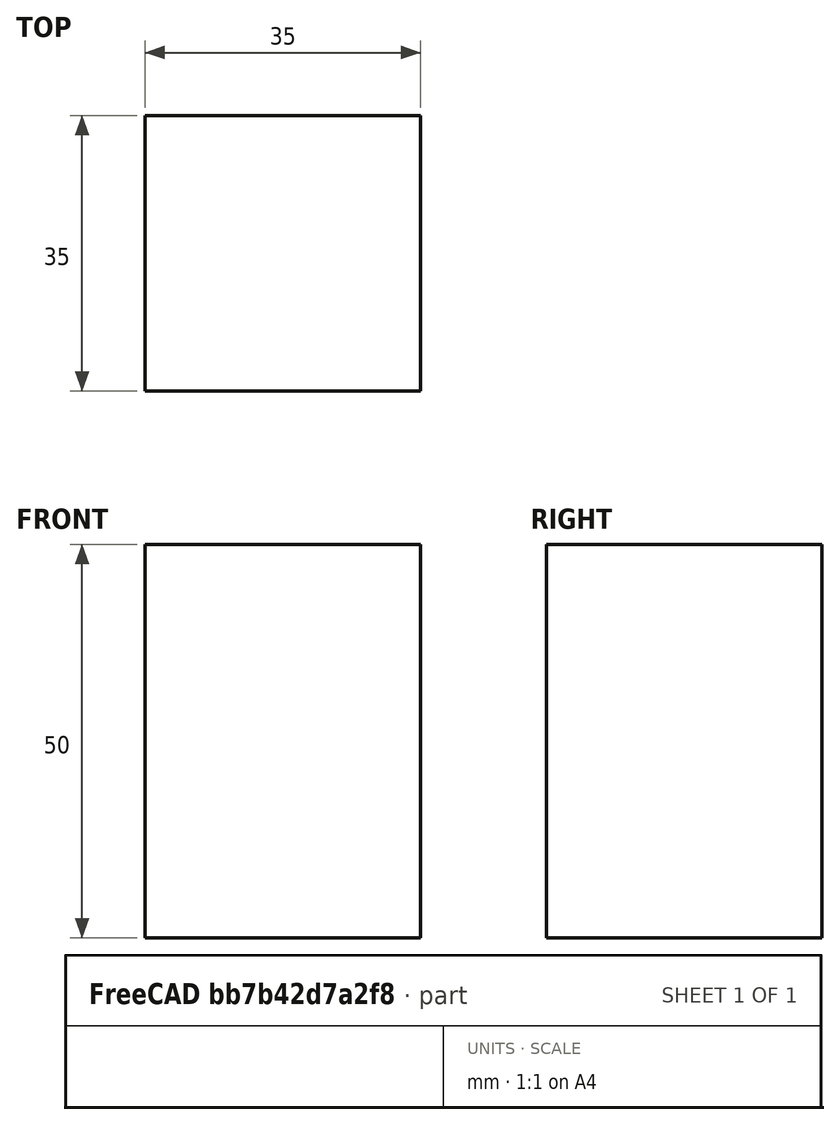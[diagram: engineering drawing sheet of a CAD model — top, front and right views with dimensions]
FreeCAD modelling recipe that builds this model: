
FCSTD DOCUMENT  (FreeCAD 0.15R4671 (Git))
Label: Square Bar 35 EN10059 S235JR
License: All rights reserved
LicenseURL: http://en.wikipedia.org/wiki/All_rights_reserved
objects: Sketcher::SketchObject×1, Part::Extrusion×1
note: 2 computed .brp shape members not serialized (recipe doc carries the construction recipe); baked Part::Feature solids carry a one-line shape summary decoded from their .brp

FEATURE [Sketcher::SketchObject] Sketch
  sketch-geometry (4):
    g0: LineSegment StartX=-17.5 StartY=-17.5 StartZ=0 EndX=17.5 EndY=-17.5 EndZ=0
    g1: LineSegment StartX=17.5 StartY=-17.5 StartZ=0 EndX=17.5 EndY=17.5 EndZ=0
    g2: LineSegment StartX=17.5 StartY=17.5 StartZ=0 EndX=-17.5 EndY=17.5 EndZ=0
    g3: LineSegment StartX=-17.5 StartY=17.5 StartZ=0 EndX=-17.5 EndY=-17.5 EndZ=0
  constraints (12):
    c: Coincident(g0,g1)
    c: Coincident(g1,g2)
    c: Coincident(g2,g3)
    c: Coincident(g3,g0)
    c: Horizontal(g0)
    c: Horizontal(g2)
    c: Vertical(g1)
    c: Vertical(g3)
    c: Symmetric(g1,g0,g-1)
    c: Symmetric(g2,g1,g-2)
    c: Equal(g1,g2)
    c: DistanceY(g1) = 35
FEATURE [Part::Extrusion] Extrude  label="Square Bar 35 EN10059 S235JR"
  Base = -> Sketch
  Dir = (0,0,50)
  Solid = true
